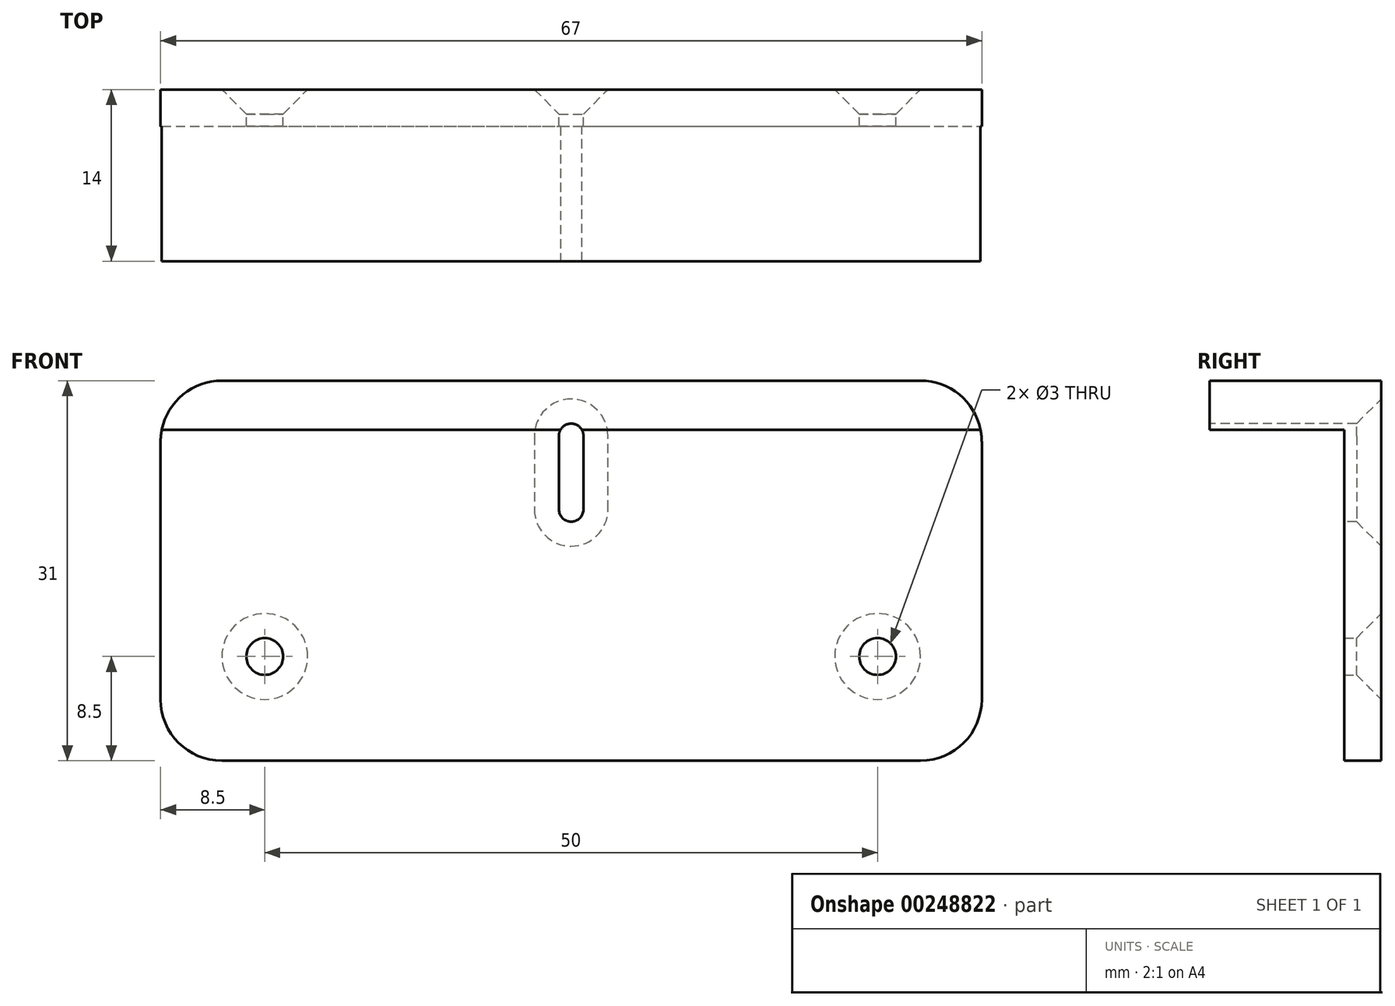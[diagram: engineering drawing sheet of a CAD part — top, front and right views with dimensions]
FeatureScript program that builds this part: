
annotation { "Feature Type Name" : "Feature", "Feature Type Description" : "" }
export const myFeature = defineFeature(function(context is Context, id is Id, definition is map)
    precondition{}
    {
        {
            var Q0;
            Q0=qCreatedBy(makeId("Front.planeOp"),FACE);
            var sketch = newSketch(context, id + "F0", { "sketchPlane" : qUnion([Q0])});
            skCircle(sketch, "E0", {"center": v(-25, 0) * mm, "radius": 1.5 * mm});
            skCircle(sketch, "E1.MirrorC", {"center": v(25, 0) * mm, "radius": 1.5 * mm});
            skLineSegment(sketch, "E2.bottom", {"start": v(-33.5, 8.5) * mm, "end": v(33.5, 8.5) * mm});
            skLineSegment(sketch, "E2.top", {"start": v(-33.5, -8.5) * mm, "end": v(33.5, -8.5) * mm});
            skLineSegment(sketch, "E2.left", {"start": v(-33.5, 8.5) * mm, "end": v(-33.5, -8.5) * mm});
            skLineSegment(sketch, "E2.right", {"start": v(33.5, 8.5) * mm, "end": v(33.5, -8.5) * mm});
            skPoint(sketch, "E2.middle", {"position": v(0, 0) * mm});
            skLineSegment(sketch, "E3", {"start": v(-33.5, 8.5) * mm, "end": v(-33.5, 18.5) * mm});
            skLineSegment(sketch, "E4", {"start": v(-33.5, 18.5) * mm, "end": v(33.5, 18.5) * mm});
            skLineSegment(sketch, "E5", {"start": v(33.5, 18.5) * mm, "end": v(33.5, 8.5) * mm});
            skLineSegment(sketch, "E6", {"start": v(-33.5, 18.5) * mm, "end": v(-33.5, 22.5) * mm});
            skLineSegment(sketch, "E7", {"start": v(-33.5, 22.5) * mm, "end": v(33.5, 22.5) * mm});
            skLineSegment(sketch, "E8", {"start": v(33.5, 22.5) * mm, "end": v(33.5, 18.5) * mm});
            skLineSegment(sketch, "E9.bottom", {"start": v(1, 19) * mm, "end": v(-1, 19) * mm});
            skLineSegment(sketch, "E9.top", {"start": v(1, 11) * mm, "end": v(-1, 11) * mm});
            skLineSegment(sketch, "E9.left", {"start": v(1, 19) * mm, "end": v(1, 11) * mm});
            skLineSegment(sketch, "E9.right", {"start": v(-1, 19) * mm, "end": v(-1, 11) * mm});
            skPoint(sketch, "E9.middle", {"position": v(0, 15) * mm});
            skSolve(sketch);
        }
        {
            var Q0;
            Q0=makeQuery(id+"F0.imprint","IMPRINT",FACE,{"disambiguationData":[TD([[makeQuery(id+"F0.imprint","IMPRINT",EDGE,{"derivedFrom":sQuery(id+"F0.wireOp",EDGE,"E2.bottom")}),1.0]])]});
            var Q1;
            Q1=makeQuery(id+"F0.imprint","IMPRINT",FACE,{"disambiguationData":[TD([[makeQuery(id+"F0.imprint","IMPRINT",EDGE,{"derivedFrom":sQuery(id+"F0.wireOp",EDGE,"E0")}),-1.0]])]});
            extrude(context, id + "F1", {"entities" : qUnion([Q0, Q1]), "depth" : 3 * mm});
        }
        {
            var Q0;
            {var subQ0=sQuery(id+"F0.wireOp",EDGE,"E6");Q0=makeQuery(id+"F0.imprint","IMPRINT",FACE,{"disambiguationData":[TD([[makeQuery(id+"F0.imprint","IMPRINT",EDGE,{"derivedFrom":subQ0}),-1.0]])]});}
            extrude(context, id + "F2", {"entities" : qUnion([Q0]), "operationType" : NewBodyOperationType.ADD, "depth" : 14 * mm});
        }
        {
            var Q0;
            Q0=makeQuery(id+"F1.opExtrude","SWEPT_EDGE",EDGE,{"disambiguationData":[OSD([sQuery(id+"F0.wireOp",EDGE,"E2.top"),sQuery(id+"F0.wireOp",EDGE,"E2.left")])]});
            var Q1;
            Q1=makeQuery(id+"F1.opExtrude","SWEPT_EDGE",EDGE,{"disambiguationData":[OSD([sQuery(id+"F0.wireOp",EDGE,"E2.top"),sQuery(id+"F0.wireOp",EDGE,"E2.right")])]});
            var Q2;
            Q2=makeQuery(id+"F2.opExtrude","SWEPT_EDGE",EDGE,{"disambiguationData":[OSD([sQuery(id+"F0.wireOp",EDGE,"E6"),sQuery(id+"F0.wireOp",EDGE,"E7")])]});
            var Q3;
            Q3=makeQuery(id+"F2.opExtrude","SWEPT_EDGE",EDGE,{"disambiguationData":[OSD([sQuery(id+"F0.wireOp",EDGE,"E7"),sQuery(id+"F0.wireOp",EDGE,"E8")])]});
            fillet(context, id + "F3", {"entities" : qUnion([Q0, Q1, Q2, Q3]), "radius" : 5 * mm, "tangentPropagation" : true, "allowEdgeOverflow" : false});
        }
        {
            var Q0;
            Q0=makeQuery(id+"F2.opExtrude","SWEPT_EDGE",EDGE,{"disambiguationData":[OSD([sQuery(id+"F0.wireOp",EDGE,"E9.bottom"),sQuery(id+"F0.wireOp",EDGE,"E9.right")])]});
            var Q1;
            Q1=makeQuery(id+"F2.opExtrude","SWEPT_EDGE",EDGE,{"disambiguationData":[OSD([sQuery(id+"F0.wireOp",EDGE,"E9.bottom"),sQuery(id+"F0.wireOp",EDGE,"E9.left")])]});
            var Q2;
            Q2=makeQuery(id+"F1.opExtrude","SWEPT_EDGE",EDGE,{"disambiguationData":[OSD([sQuery(id+"F0.wireOp",EDGE,"E9.top"),sQuery(id+"F0.wireOp",EDGE,"E9.left")])]});
            var Q3;
            Q3=makeQuery(id+"F1.opExtrude","SWEPT_EDGE",EDGE,{"disambiguationData":[OSD([sQuery(id+"F0.wireOp",EDGE,"E9.top"),sQuery(id+"F0.wireOp",EDGE,"E9.right")])]});
            fillet(context, id + "F4", {"entities" : qUnion([Q0, Q1, Q2, Q3]), "radius" : 1 * mm, "tangentPropagation" : true, "allowEdgeOverflow" : false});
        }
        {
            var Q0;
            Q0=makeQuery(id+"F1.opExtrude","CAP_EDGE",EDGE,{"disambiguationData":[OSD([sQuery(id+"F0.wireOp",EDGE,"E0")])],"isStart":true});
            var Q1;
            Q1=makeQuery(id+"F1.opExtrude","CAP_EDGE",EDGE,{"disambiguationData":[OSD([sQuery(id+"F0.wireOp",EDGE,"E1.MirrorC")])],"isStart":true});
            var Q2;
            {var subQ0=sQuery(id+"F0.wireOp",EDGE,"E9.right");Q2=makeQuery(id+"F2.boolean.opBoolean","MERGE",EDGE,{"derivedFrom":[makeQuery(id+"F1.opExtrude","CAP_EDGE",EDGE,{"disambiguationData":[OSD([subQ0])],"isStart":true}),makeQuery(id+"F2.opExtrude","CAP_EDGE",EDGE,{"disambiguationData":[OSD([subQ0])],"isStart":true})]});}
            chamfer(context, id + "F5", {"entities" : qUnion([Q0, Q1, Q2]), "width" : 2 * mm, "tangentPropagation" : true});
        }
    });
